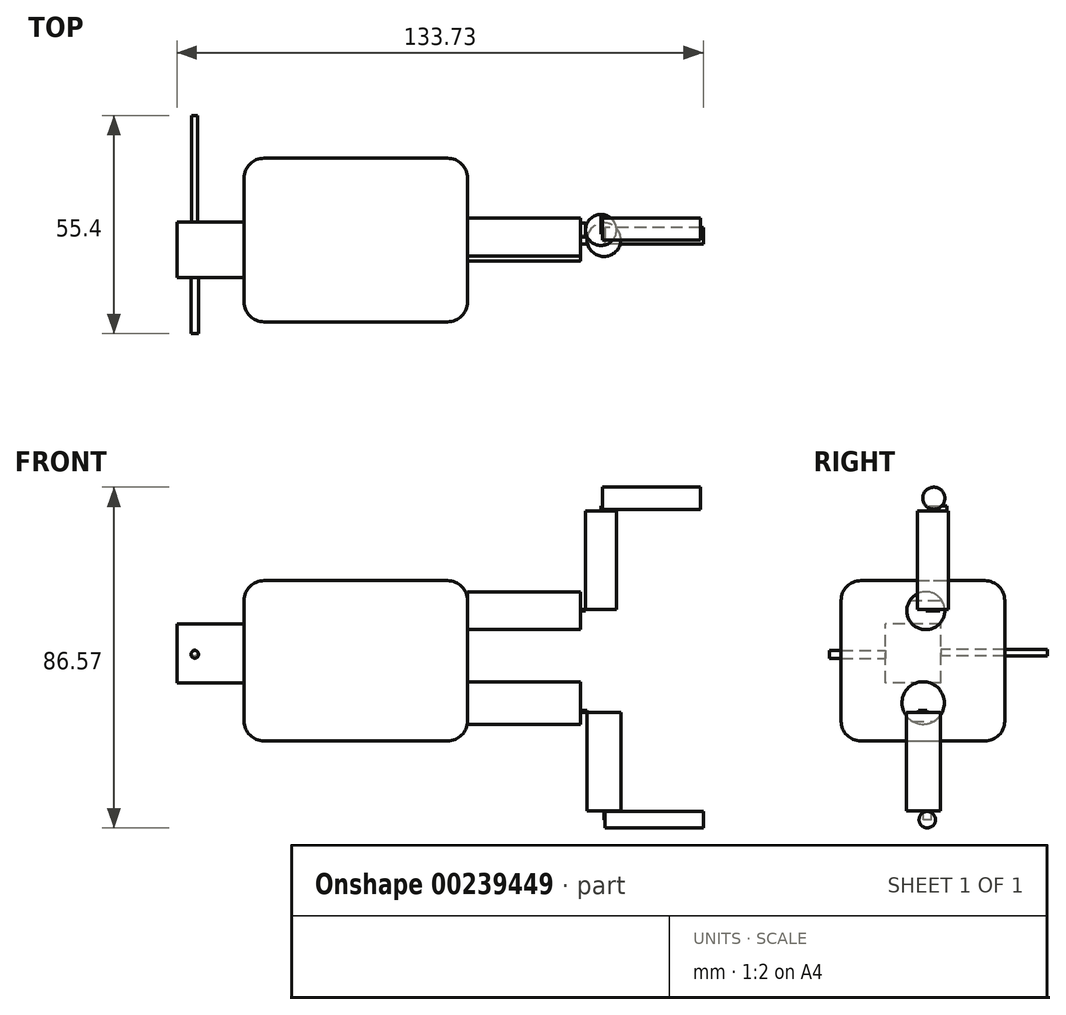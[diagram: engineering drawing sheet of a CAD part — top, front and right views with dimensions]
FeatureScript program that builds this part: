
annotation { "Feature Type Name" : "Feature", "Feature Type Description" : "" }
export const myFeature = defineFeature(function(context is Context, id is Id, definition is map)
    precondition{}
    {
        {
            var Q0;
            Q0=qCreatedBy(makeId("Top.planeOp"),FACE);
            var sketch = newSketch(context, id + "F0", { "sketchPlane" : qUnion([Q0])});
            skLineSegment(sketch, "E0.bottom", {"start": v(-23.58, -17.27) * mm, "end": v(33.13, -17.27) * mm});
            skLineSegment(sketch, "E0.top", {"start": v(-23.58, 24.28) * mm, "end": v(33.13, 24.28) * mm});
            skLineSegment(sketch, "E0.left", {"start": v(-23.58, -17.27) * mm, "end": v(-23.58, 24.28) * mm});
            skLineSegment(sketch, "E0.right", {"start": v(33.13, -17.27) * mm, "end": v(33.13, 24.28) * mm});
            skSolve(sketch);
        }
        {
            var Q0;
            Q0=makeQuery(id+"F0.imprint","IMPRINT",FACE,{"disambiguationData":[TD([[makeQuery(id+"F0.imprint","IMPRINT",EDGE,{"derivedFrom":sQuery(id+"F0.wireOp",EDGE,"E0.bottom")}),1.0]])]});
            extrude(context, id + "F1", {"entities" : qUnion([Q0]), "depth" : 40.7 * mm});
        }
        {
            var Q0;
            Q0=makeQuery(id+"F1.opExtrude","SWEPT_EDGE",EDGE,{"disambiguationData":[OSD([sQuery(id+"F0.wireOp",EDGE,"E0.top"),sQuery(id+"F0.wireOp",EDGE,"E0.left")])]});
            var Q1;
            Q1=makeQuery(id+"F1.opExtrude","CAP_EDGE",EDGE,{"disambiguationData":[OSD([sQuery(id+"F0.wireOp",EDGE,"E0.top")])],"isStart":true});
            var Q2;
            Q2=makeQuery(id+"F1.opExtrude","CAP_EDGE",EDGE,{"disambiguationData":[OSD([sQuery(id+"F0.wireOp",EDGE,"E0.left")])],"isStart":true});
            var Q3;
            Q3=makeQuery(id+"F1.opExtrude","CAP_EDGE",EDGE,{"disambiguationData":[OSD([sQuery(id+"F0.wireOp",EDGE,"E0.top")])],"isStart":false});
            var Q4;
            Q4=makeQuery(id+"F1.opExtrude","SWEPT_EDGE",EDGE,{"disambiguationData":[OSD([sQuery(id+"F0.wireOp",EDGE,"E0.top"),sQuery(id+"F0.wireOp",EDGE,"E0.right")])]});
            var Q5;
            Q5=makeQuery(id+"F1.opExtrude","CAP_EDGE",EDGE,{"disambiguationData":[OSD([sQuery(id+"F0.wireOp",EDGE,"E0.left")])],"isStart":false});
            var Q6;
            Q6=makeQuery(id+"F1.opExtrude","CAP_EDGE",EDGE,{"disambiguationData":[OSD([sQuery(id+"F0.wireOp",EDGE,"E0.right")])],"isStart":false});
            var Q7;
            Q7=makeQuery(id+"F1.opExtrude","SWEPT_EDGE",EDGE,{"disambiguationData":[OSD([sQuery(id+"F0.wireOp",EDGE,"E0.bottom"),sQuery(id+"F0.wireOp",EDGE,"E0.left")])]});
            var Q8;
            Q8=makeQuery(id+"F1.opExtrude","CAP_EDGE",EDGE,{"disambiguationData":[OSD([sQuery(id+"F0.wireOp",EDGE,"E0.bottom")])],"isStart":false});
            var Q9;
            Q9=makeQuery(id+"F1.opExtrude","CAP_EDGE",EDGE,{"disambiguationData":[OSD([sQuery(id+"F0.wireOp",EDGE,"E0.right")])],"isStart":true});
            var Q10;
            Q10=makeQuery(id+"F1.opExtrude","CAP_EDGE",EDGE,{"disambiguationData":[OSD([sQuery(id+"F0.wireOp",EDGE,"E0.bottom")])],"isStart":true});
            var Q11;
            Q11=makeQuery(id+"F1.opExtrude","SWEPT_EDGE",EDGE,{"disambiguationData":[OSD([sQuery(id+"F0.wireOp",EDGE,"E0.bottom"),sQuery(id+"F0.wireOp",EDGE,"E0.right")])]});
            fillet(context, id + "F2", {"entities" : qUnion([Q0, Q1, Q2, Q3, Q4, Q5, Q6, Q7, Q8, Q9, Q10, Q11]), "radius" : 5 * mm, "tangentPropagation" : true, "allowEdgeOverflow" : false});
        }
        {
            var Q0;
            Q0=makeQuery(id+"F1.opExtrude","SWEPT_FACE",FACE,{"disambiguationData":[OSD([sQuery(id+"F0.wireOp",EDGE,"E0.left")])]});
            var sketch = newSketch(context, id + "F3", { "sketchPlane" : qUnion([Q0])});
            skLineSegment(sketch, "E1.bottom", {"start": v(-8.11, 14.74) * mm, "end": v(5.98, 14.74) * mm});
            skLineSegment(sketch, "E1.top", {"start": v(-8.11, 29.69) * mm, "end": v(5.98, 29.69) * mm});
            skLineSegment(sketch, "E1.left", {"start": v(-8.11, 14.74) * mm, "end": v(-8.11, 29.69) * mm});
            skLineSegment(sketch, "E1.right", {"start": v(5.98, 14.74) * mm, "end": v(5.98, 29.69) * mm});
            skSolve(sketch);
        }
        {
            var Q0;
            Q0=makeQuery(id+"F3.imprint","IMPRINT",FACE,{"disambiguationData":[TD([[makeQuery(id+"F3.imprint","IMPRINT",EDGE,{"derivedFrom":sQuery(id+"F3.wireOp",EDGE,"E1.bottom")}),1.0]])]});
            extrude(context, id + "F4", {"entities" : qUnion([Q0]), "operationType" : NewBodyOperationType.ADD, "depth" : 17.1 * mm});
        }
        {
            var Q0;
            Q0=makeQuery(id+"F4.opExtrude","SWEPT_FACE",FACE,{"disambiguationData":[OSD([sQuery(id+"F3.wireOp",EDGE,"E1.right")])]});
            var sketch = newSketch(context, id + "F5", { "sketchPlane" : qUnion([Q0])});
            skCircle(sketch, "E2", {"center": v(-36.21, 22.4) * mm, "radius": 0.8 * mm});
            skSolve(sketch);
        }
        {
            var Q0;
            Q0=makeQuery(id+"F5.imprint","IMPRINT",FACE,{"disambiguationData":[TD([[makeQuery(id+"F5.imprint","IMPRINT",EDGE,{"derivedFrom":sQuery(id+"F5.wireOp",EDGE,"E2")}),1.0]])]});
            extrude(context, id + "F6", {"entities" : qUnion([Q0]), "operationType" : NewBodyOperationType.ADD, "oppositeDirection" : true, "depth" : 41.1 * mm});
        }
        {
            var Q0;
            Q0=makeQuery(id+"F4.opExtrude","SWEPT_FACE",FACE,{"disambiguationData":[OSD([sQuery(id+"F3.wireOp",EDGE,"E1.right")])]});
            var sketch = newSketch(context, id + "F7", { "sketchPlane" : qUnion([Q0])});
            skCircle(sketch, "E3", {"center": v(-36.13, 21.96) * mm, "radius": 0.97 * mm});
            skSolve(sketch);
        }
        {
            var Q0;
            Q0=makeQuery(id+"F7.imprint","IMPRINT",FACE,{"disambiguationData":[TD([[makeQuery(id+"F7.imprint","IMPRINT",EDGE,{"derivedFrom":sQuery(id+"F7.wireOp",EDGE,"E3")}),1.0]])]});
            extrude(context, id + "F8", {"entities" : qUnion([Q0]), "operationType" : NewBodyOperationType.ADD, "depth" : 14.3 * mm});
        }
        {
            var Q0;
            Q0=makeQuery(id+"F8.opExtrude","CAP_FACE",FACE,{"disambiguationData":[OSD([sQuery(id+"F7.wireOp",EDGE,"E3")])],"isStart":false});
            var sketch = newSketch(context, id + "F9", { "sketchPlane" : qUnion([Q0])});
            skArc(sketch, "E4", {"start": v(-36.1, 22.93) * mm, "mid": v(-44.04, 23.01) * mm, "end": v(-36.35, 21.02) * mm});
            skSolve(sketch);
        }
        {
            var Q0;
            Q0=makeQuery(id+"F1.opExtrude","SWEPT_FACE",FACE,{"disambiguationData":[OSD([sQuery(id+"F0.wireOp",EDGE,"E0.right")])]});
            var sketch = newSketch(context, id + "F10", { "sketchPlane" : qUnion([Q0])});
            skCircle(sketch, "E5", {"center": v(4.26, 33.07) * mm, "radius": 4.81 * mm});
            skCircle(sketch, "E6", {"center": v(3.57, 9.63) * mm, "radius": 5.4 * mm});
            skSolve(sketch);
        }
        {
            var Q0;
            Q0 = qSketchRegion(id + "F10", true);
            extrude(context, id + "F11", {"entities" : qUnion([Q0]), "operationType" : NewBodyOperationType.ADD, "depth" : 28.7 * mm});
        }
        {
            var Q0;
            Q0=makeQuery(id+"F11.opExtrude","CAP_FACE",FACE,{"disambiguationData":[OSD([sQuery(id+"F10.wireOp",EDGE,"E5")])],"isStart":false});
            var sketch = newSketch(context, id + "F12", { "sketchPlane" : qUnion([Q0])});
            skLineSegment(sketch, "E7.bottom", {"start": v(4.26, 33.07) * mm, "end": v(7.84, 33.07) * mm});
            skLineSegment(sketch, "E7.top", {"start": v(4.26, 33.43) * mm, "end": v(7.84, 33.43) * mm});
            skLineSegment(sketch, "E7.left", {"start": v(4.26, 33.07) * mm, "end": v(4.26, 33.43) * mm});
            skLineSegment(sketch, "E7.right", {"start": v(7.84, 33.07) * mm, "end": v(7.84, 33.43) * mm});
            skSolve(sketch);
        }
        {
            var Q0;
            Q0 = qSketchRegion(id + "F12", true);
            extrude(context, id + "F13", {"entities" : qUnion([Q0]), "operationType" : NewBodyOperationType.ADD, "depth" : 1.3 * mm});
        }
        {
            var Q0;
            Q0=makeQuery(id+"F13.opExtrude","SWEPT_FACE",FACE,{"disambiguationData":[OSD([sQuery(id+"F12.wireOp",EDGE,"E7.top")])]});
            var sketch = newSketch(context, id + "F14", { "sketchPlane" : qUnion([Q0])});
            skCircle(sketch, "E8", {"center": v(67.07, 6.05) * mm, "radius": 3.94 * mm});
            skPoint(sketch, "E8.first.point", {"position": v(63.13, 6.05) * mm});
            skPoint(sketch, "E8.second.point", {"position": v(71, 6.05) * mm});
            skPoint(sketch, "E8.second.point.positionSnap0", {"position": v(63.13, 6.05) * mm});
            skPoint(sketch, "E8.third.point", {"position": v(68.36, 9.77) * mm});
            skSolve(sketch);
        }
        {
            var Q0;
            Q0 = qSketchRegion(id + "F14", true);
            extrude(context, id + "F15", {"entities" : qUnion([Q0]), "depth" : 25 * mm});
        }
        {
            var Q0;
            Q0=makeQuery(id+"F11.opExtrude","CAP_FACE",FACE,{"disambiguationData":[OSD([sQuery(id+"F10.wireOp",EDGE,"E6")])],"isStart":false});
            var sketch = newSketch(context, id + "F16", { "sketchPlane" : qUnion([Q0])});
            skLineSegment(sketch, "E9.bottom", {"start": v(2.43, 7.17) * mm, "end": v(4.59, 7.17) * mm});
            skLineSegment(sketch, "E9.top", {"start": v(2.43, 7.74) * mm, "end": v(4.59, 7.74) * mm});
            skLineSegment(sketch, "E9.left", {"start": v(2.43, 7.17) * mm, "end": v(2.43, 7.74) * mm});
            skLineSegment(sketch, "E9.right", {"start": v(4.59, 7.17) * mm, "end": v(4.59, 7.74) * mm});
            skSolve(sketch);
        }
        {
            var Q0;
            Q0 = qSketchRegion(id + "F16", true);
            extrude(context, id + "F17", {"entities" : qUnion([Q0]), "operationType" : NewBodyOperationType.ADD, "depth" : 1.7 * mm});
        }
        {
            var Q0;
            Q0=makeQuery(id+"F17.opExtrude","SWEPT_FACE",FACE,{"disambiguationData":[OSD([sQuery(id+"F16.wireOp",EDGE,"E9.bottom")])]});
            var sketch = newSketch(context, id + "F18", { "sketchPlane" : qUnion([Q0])});
            skCircle(sketch, "E10", {"center": v(67.82, -3.61) * mm, "radius": 4.3 * mm});
            skPoint(sketch, "E10.first.point", {"position": v(63.53, -3.5) * mm});
            skPoint(sketch, "E10.second.point", {"position": v(72.1, -3.5) * mm});
            skPoint(sketch, "E10.second.point.positionSnap0", {"position": v(63.53, -3.5) * mm});
            skPoint(sketch, "E10.third.point", {"position": v(68.95, 0.53) * mm});
            skSolve(sketch);
        }
        {
            var Q0;
            Q0 = qSketchRegion(id + "F18", true);
            extrude(context, id + "F19", {"entities" : qUnion([Q0]), "operationType" : NewBodyOperationType.ADD, "depth" : 25 * mm});
        }
        {
            var Q0;
            Q0=makeQuery(id+"F19.opExtrude","CAP_FACE",FACE,{"disambiguationData":[OSD([sQuery(id+"F18.wireOp",EDGE,"E10")])],"isStart":false});
            var sketch = newSketch(context, id + "F20", { "sketchPlane" : qUnion([Q0])});
            skLineSegment(sketch, "E11.bottom", {"start": v(68.05, -5.63) * mm, "end": v(67.82, -5.63) * mm});
            skLineSegment(sketch, "E11.top", {"start": v(68.05, -3.61) * mm, "end": v(67.82, -3.61) * mm});
            skLineSegment(sketch, "E11.left", {"start": v(68.05, -5.63) * mm, "end": v(68.05, -3.61) * mm});
            skLineSegment(sketch, "E11.right", {"start": v(67.82, -5.63) * mm, "end": v(67.82, -3.61) * mm});
            skSolve(sketch);
        }
        {
            var Q0;
            Q0 = qSketchRegion(id + "F20", true);
            extrude(context, id + "F21", {"entities" : qUnion([Q0]), "operationType" : NewBodyOperationType.ADD, "depth" : 2.2 * mm});
        }
        {
            var Q0;
            Q0=makeQuery(id+"F21.opExtrude","SWEPT_FACE",FACE,{"disambiguationData":[OSD([sQuery(id+"F20.wireOp",EDGE,"E11.left")])]});
            var sketch = newSketch(context, id + "F22", { "sketchPlane" : qUnion([Q0])});
            skCircle(sketch, "E12", {"center": v(4.62, -20.03) * mm, "radius": 2.08 * mm});
            skSolve(sketch);
        }
        {
            var Q0;
            Q0 = qSketchRegion(id + "F22", true);
            extrude(context, id + "F23", {"entities" : qUnion([Q0]), "operationType" : NewBodyOperationType.ADD, "depth" : 25 * mm});
        }
        {
            var Q0;
            Q0=makeQuery(id+"F15.opExtrude","CAP_FACE",FACE,{"disambiguationData":[OSD([sQuery(id+"F14.wireOp",EDGE,"E8")])],"isStart":false});
            var sketch = newSketch(context, id + "F24", { "sketchPlane" : qUnion([Q0])});
            skLineSegment(sketch, "E13.bottom", {"start": v(67.12, 5.02) * mm, "end": v(67.38, 5.02) * mm});
            skLineSegment(sketch, "E13.top", {"start": v(67.12, 9.6) * mm, "end": v(67.38, 9.6) * mm});
            skLineSegment(sketch, "E13.left", {"start": v(67.12, 5.02) * mm, "end": v(67.12, 9.6) * mm});
            skLineSegment(sketch, "E13.right", {"start": v(67.38, 5.02) * mm, "end": v(67.38, 9.6) * mm});
            skSolve(sketch);
        }
        {
            var Q0;
            Q0 = qSketchRegion(id + "F24", true);
            extrude(context, id + "F25", {"entities" : qUnion([Q0]), "operationType" : NewBodyOperationType.ADD, "depth" : 1.2 * mm});
        }
        {
            var Q0;
            Q0=makeQuery(id+"F25.opExtrude","SWEPT_FACE",FACE,{"disambiguationData":[OSD([sQuery(id+"F24.wireOp",EDGE,"E13.right")])]});
            var sketch = newSketch(context, id + "F26", { "sketchPlane" : qUnion([Q0])});
            skCircle(sketch, "E14", {"center": v(6.29, 61.66) * mm, "radius": 2.8 * mm});
            skPoint(sketch, "E14.first.point", {"position": v(6.68, 58.88) * mm});
            skPoint(sketch, "E14.second.point", {"position": v(6.47, 64.46) * mm});
            skPoint(sketch, "E14.third.point", {"position": v(9.09, 61.8) * mm});
            skSolve(sketch);
        }
        {
            var Q0;
            Q0 = qSketchRegion(id + "F26", true);
            extrude(context, id + "F27", {"entities" : qUnion([Q0]), "operationType" : NewBodyOperationType.ADD, "depth" : 25 * mm});
        }
    });
